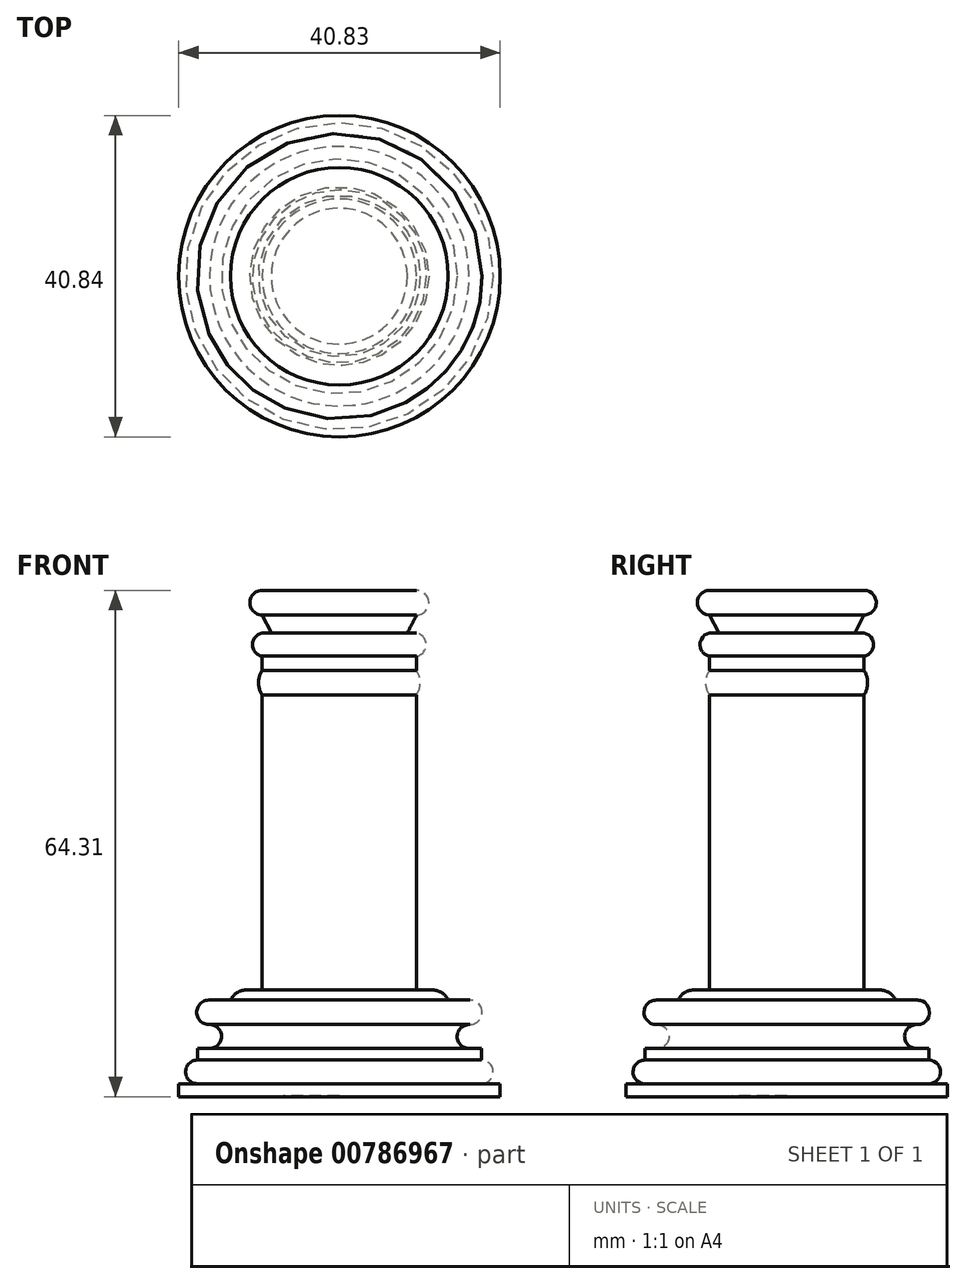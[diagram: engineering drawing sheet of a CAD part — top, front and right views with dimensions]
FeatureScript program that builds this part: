
annotation { "Feature Type Name" : "Feature", "Feature Type Description" : "" }
export const myFeature = defineFeature(function(context is Context, id is Id, definition is map)
    precondition{}
    {
        {
            var Q0;
            Q0=qCreatedBy(makeId("Front.planeOp"),FACE);
            var sketch = newSketch(context, id + "F0", { "sketchPlane" : qUnion([Q0])});
            skLineSegment(sketch, "E0", {"start": v(-9.82, 0) * mm, "end": v(-19.63, 0) * mm});
            skPoint(sketch, "E1.visualSharp", {"position": v(-21.8, 0) * mm});
            skArc(sketch, "E2", {"start": v(-19.63, 0) * mm, "mid": v(-21.19, -1.55) * mm, "end": v(-19.63, -3.1) * mm});
            skPoint(sketch, "E3.2.internal.orphan", {"position": v(-19.63, -5.41) * mm});
            skArc(sketch, "E4", {"start": v(-19.63, -5.41) * mm, "mid": v(-20.84, -6.88) * mm, "end": v(-19.63, -8.36) * mm});
            skLineSegment(sketch, "E5", {"start": v(-19.63, -8.36) * mm, "end": v(-19.63, -10.15) * mm});
            skLineSegment(sketch, "E6", {"start": v(-27.85, -62.66) * mm, "end": v(-30.23, -62.66) * mm});
            skLineSegment(sketch, "E7", {"start": v(-30.23, -62.66) * mm, "end": v(-30.23, -64.3) * mm});
            skLineSegment(sketch, "E8", {"start": v(-30.23, -64.3) * mm, "end": v(-9.82, -64.2) * mm});
            skArc(sketch, "E9", {"start": v(-27.85, -59.66) * mm, "mid": v(-29.35, -61.16) * mm, "end": v(-27.85, -62.66) * mm});
            skLineSegment(sketch, "E10", {"start": v(-27.85, -59.66) * mm, "end": v(-27.85, -58.19) * mm});
            skLineSegment(sketch, "E11", {"start": v(-27.85, -58.19) * mm, "end": v(-26.3, -58.19) * mm});
            skArc(sketch, "E12", {"start": v(-26.3, -58.19) * mm, "mid": v(-24.78, -56.67) * mm, "end": v(-26.3, -55.15) * mm});
            skArc(sketch, "E13", {"start": v(-26.3, -52.05) * mm, "mid": v(-27.95, -53.6) * mm, "end": v(-26.3, -55.15) * mm});
            skLineSegment(sketch, "E14", {"start": v(-26.3, -52.05) * mm, "end": v(-23.64, -52.05) * mm});
            skLineSegment(sketch, "E15", {"start": v(-23.64, -52.05) * mm, "end": v(-23.64, -50.76) * mm});
            skLineSegment(sketch, "E16", {"start": v(-9.82, 0) * mm, "end": v(-9.82, -64.2) * mm});
            skPoint(sketch, "E17.orphan", {"position": v(0, 0) * mm});
            skPoint(sketch, "E18.orphan", {"position": v(0, -64.15) * mm});
            skArc(sketch, "E19", {"start": v(-19.63, -10.15) * mm, "mid": v(-20.09, -11.71) * mm, "end": v(-19.63, -13.28) * mm});
            skLineSegment(sketch, "E20", {"start": v(-19.63, -13.28) * mm, "end": v(-19.63, -50.76) * mm});
            skLineSegment(sketch, "E21", {"start": v(-23.64, -50.76) * mm, "end": v(-19.63, -50.76) * mm});
            skLineSegment(sketch, "E22", {"start": v(-19.63, -3.1) * mm, "end": v(-18.45, -5.41) * mm});
            skLineSegment(sketch, "E23", {"start": v(-18.45, -5.41) * mm, "end": v(-19.63, -5.41) * mm});
            skSolve(sketch);
        }
        {
            var Q0;
            Q0=makeQuery(id+"F0.imprint","IMPRINT",FACE,{"disambiguationData":[TD([[makeQuery(id+"F0.imprint","IMPRINT",EDGE,{"derivedFrom":sQuery(id+"F0.wireOp",EDGE,"E0")}),1.0]])]});
            var Q1;
            Q1=sQuery(id+"F0.wireOp",EDGE,"E16");
            revolve(context, id + "F1", {"surfaceOperationType" : NewSurfaceOperationType.NEW, "entities" : qUnion([Q0]), "axis" : qUnion([Q1]), "revolveType" : RevolveType.FULL});
        }
        {
            var Q0;
            Q0=makeQuery(id+"F1.opRevolve","SWEPT_EDGE",EDGE,{"disambiguationData":[OSD([sQuery(id+"F0.wireOp",EDGE,"E15"),sQuery(id+"F0.wireOp",EDGE,"E21")])]});
            fillet(context, id + "F2", {"entities" : qUnion([Q0]), "radius" : 2.2 * mm, "tangentPropagation" : true, "allowEdgeOverflow" : false});
        }
        {
            var Q0;
            Q0=makeQuery(id+"F1.opRevolve","SWEPT_EDGE",EDGE,{"disambiguationData":[OSD([sQuery(id+"F0.wireOp",EDGE,"E13"),sQuery(id+"F0.wireOp",EDGE,"E14")])]});
            fillet(context, id + "F3", {"entities" : qUnion([Q0]), "radius" : 156.34 * mm, "tangentPropagation" : true, "allowEdgeOverflow" : false});
        }
    });
